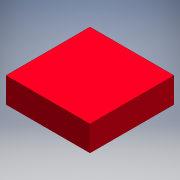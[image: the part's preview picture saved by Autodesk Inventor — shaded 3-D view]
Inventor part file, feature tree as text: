
AUTODESK INVENTOR PART (.ipt)
format: ipt  version: 2016 (Build 200138000, 138)  size: 92,672 bytes
history: native  units: mm
features: extrude x1, sketch x1
ambient origin geometry x8: Origin, YZ Plane, XZ Plane, XY Plane, X Axis, Y Axis, Z Axis, Center Point
bodies: Solid1 (feature_tree)
feature tree (2):
  extrude  "Extrusion1"  Depth=10.0mm
  sketch  "Sketch1"  dims[d0=10.0mm d1=10.0mm d2=5.0mm d3=5.0mm d4=3.0mm d5=0.0mm]
